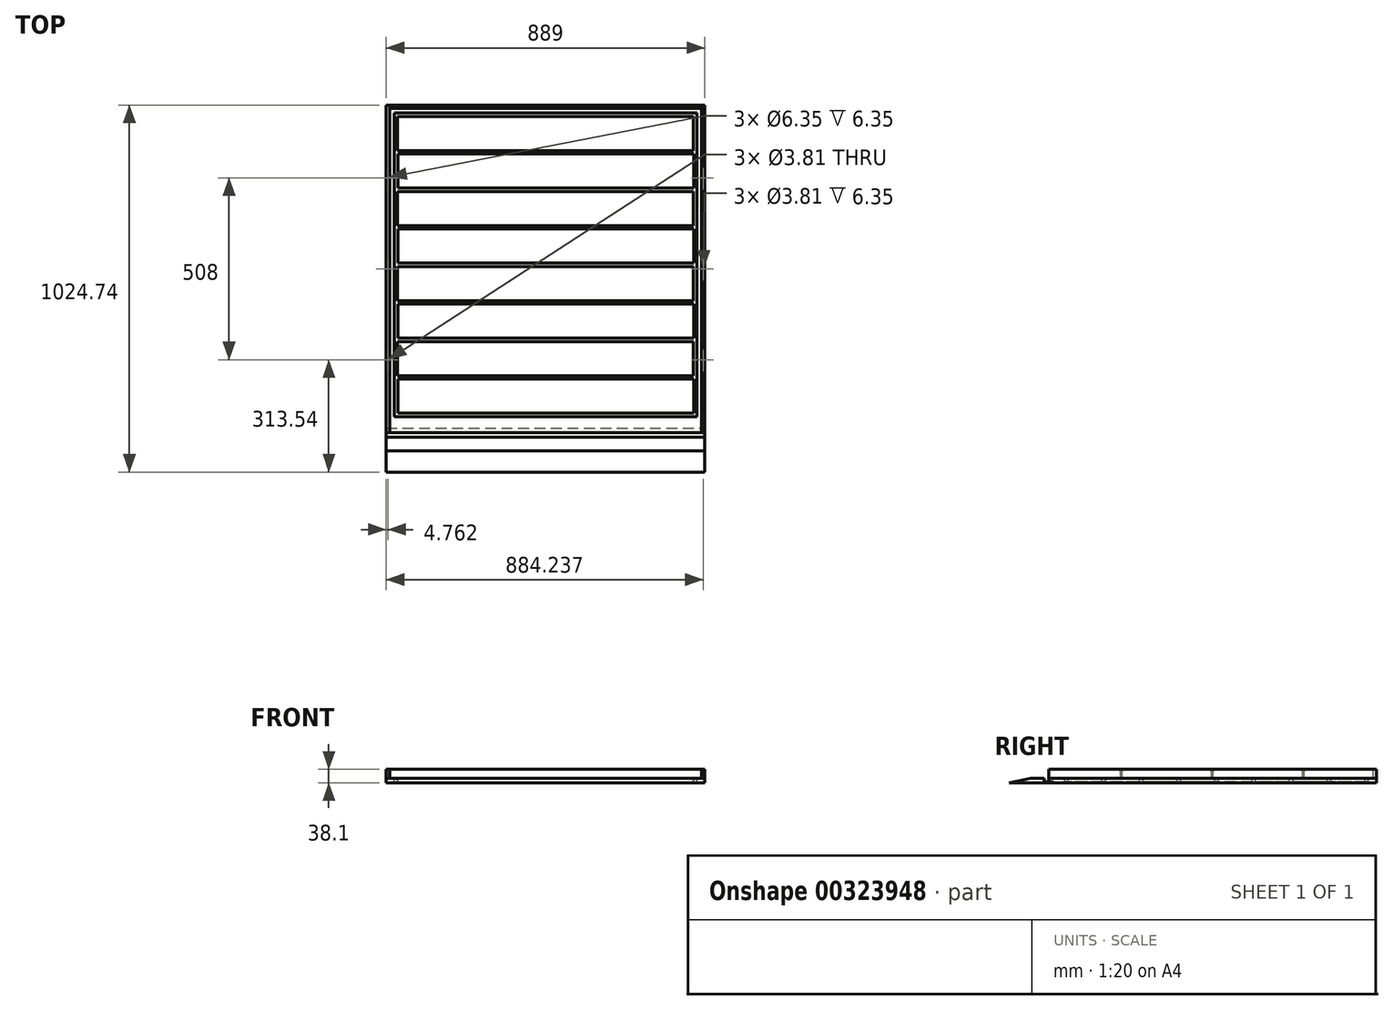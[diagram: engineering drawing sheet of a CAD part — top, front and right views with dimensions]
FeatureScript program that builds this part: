
annotation { "Feature Type Name" : "Feature", "Feature Type Description" : "" }
export const myFeature = defineFeature(function(context is Context, id is Id, definition is map)
    precondition{}
    {
        {
            var Q0;
            Q0=qCreatedBy(makeId("Top.planeOp"),FACE);
            var sketch = newSketch(context, id + "F0", { "sketchPlane" : qUnion([Q0])});
            skLineSegment(sketch, "E0.bottom", {"start": v(-444.5, 457.2) * mm, "end": v(444.5, 457.2) * mm});
            skLineSegment(sketch, "E0.top", {"start": v(-444.5, -457.2) * mm, "end": v(444.5, -457.2) * mm});
            skLineSegment(sketch, "E0.left", {"start": v(-444.5, 457.2) * mm, "end": v(-444.5, -457.2) * mm});
            skLineSegment(sketch, "E0.right", {"start": v(444.5, 457.2) * mm, "end": v(444.5, -457.2) * mm});
            skSolve(sketch);
        }
        {
            var Q0;
            Q0=makeQuery(id+"F0.imprint","IMPRINT",FACE,{"disambiguationData":[TD([[makeQuery(id+"F0.imprint","IMPRINT",EDGE,{"derivedFrom":sQuery(id+"F0.wireOp",EDGE,"E0.bottom")}),-1.0]])]});
            extrude(context, id + "F1", {"entities" : qUnion([Q0]), "depth" : 12.7 * mm});
        }
        {
            var Q0;
            Q0=makeQuery(id+"F1.opExtrude","SWEPT_FACE",FACE,{"disambiguationData":[OSD([sQuery(id+"F0.wireOp",EDGE,"E0.right")])]});
            var sketch = newSketch(context, id + "F2", { "sketchPlane" : qUnion([Q0])});
            skLineSegment(sketch, "E1", {"start": v(-457.2, 0) * mm, "end": v(-457.2, 3.17) * mm});
            skLineSegment(sketch, "E2", {"start": v(-457.2, 3.17) * mm, "end": v(-444.5, 3.17) * mm});
            skLineSegment(sketch, "E3", {"start": v(-444.5, 3.17) * mm, "end": v(-444.5, 0) * mm});
            skLineSegment(sketch, "E4", {"start": v(-457.2, 0) * mm, "end": v(-444.5, 0) * mm});
            skSolve(sketch);
        }
        {
            var Q0;
            Q0=makeQuery(id+"F2.imprint","IMPRINT",FACE,{"disambiguationData":[TD([[makeQuery(id+"F2.imprint","IMPRINT",EDGE,{"derivedFrom":sQuery(id+"F2.wireOp",EDGE,"E1")}),1.0]])]});
            extrude(context, id + "F3", {"entities" : qUnion([Q0]), "operationType" : NewBodyOperationType.REMOVE, "endBound" : BoundingType.THROUGH_ALL, "oppositeDirection" : true, "depth" : 25.4 * mm});
        }
        {
            var Q0;
            Q0=makeQuery(id+"F1.opExtrude","SWEPT_FACE",FACE,{"disambiguationData":[OSD([sQuery(id+"F0.wireOp",EDGE,"E0.right")])]});
            var sketch = newSketch(context, id + "F4", { "sketchPlane" : qUnion([Q0])});
            skLineSegment(sketch, "E5", {"start": v(-508, 12.7) * mm, "end": v(-567.54, 0) * mm});
            skLineSegment(sketch, "E6", {"start": v(-469.9, 12.7) * mm, "end": v(-469.9, 3.18) * mm});
            skLineSegment(sketch, "E7", {"start": v(-508, 12.7) * mm, "end": v(-469.9, 12.7) * mm});
            skLineSegment(sketch, "E8", {"start": v(-469.9, 3.18) * mm, "end": v(-444.5, 3.18) * mm});
            skLineSegment(sketch, "E9", {"start": v(-444.5, 3.18) * mm, "end": v(-444.5, 0) * mm});
            skLineSegment(sketch, "E10", {"start": v(-444.5, 0) * mm, "end": v(-567.54, 0) * mm});
            skSolve(sketch);
        }
        {
            var Q0;
            Q0=makeQuery(id+"F4.imprint","IMPRINT",FACE,{"disambiguationData":[TD([[makeQuery(id+"F4.imprint","IMPRINT",EDGE,{"derivedFrom":sQuery(id+"F4.wireOp",EDGE,"E5")}),1.0]])]});
            var Q1;
            Q1=makeQuery(id+"F1.opExtrude","SWEPT_FACE",FACE,{"disambiguationData":[OSD([sQuery(id+"F0.wireOp",EDGE,"E0.left")])]});
            extrude(context, id + "F5", {"entities" : qUnion([Q0]), "endBound" : BoundingType.UP_TO_SURFACE, "oppositeDirection" : true, "endBoundEntityFace" : qUnion([Q1]), "depth" : 25.4 * mm});
        }
        {
            var Q0;
            Q0=makeQuery(id+"F1.opExtrude","CAP_FACE",FACE,{"disambiguationData":[OSD([sQuery(id+"F0.wireOp",EDGE,"E0.bottom"),sQuery(id+"F0.wireOp",EDGE,"E0.top"),sQuery(id+"F0.wireOp",EDGE,"E0.left"),sQuery(id+"F0.wireOp",EDGE,"E0.right")])],"isStart":false});
            var sketch = newSketch(context, id + "F6", { "sketchPlane" : qUnion([Q0])});
            skLineSegment(sketch, "E11.bottom", {"start": v(444.5, -457.2) * mm, "end": v(434.98, -457.2) * mm});
            skLineSegment(sketch, "E11.top", {"start": v(444.5, 457.2) * mm, "end": v(434.98, 457.2) * mm});
            skLineSegment(sketch, "E11.left", {"start": v(444.5, -457.2) * mm, "end": v(444.5, 457.2) * mm});
            skLineSegment(sketch, "E11.right", {"start": v(434.98, -457.2) * mm, "end": v(434.98, 457.2) * mm});
            skLineSegment(sketch, "E12.bottom", {"start": v(-444.5, -457.2) * mm, "end": v(-434.98, -457.2) * mm});
            skLineSegment(sketch, "E12.top", {"start": v(-444.5, 457.2) * mm, "end": v(-434.98, 457.2) * mm});
            skLineSegment(sketch, "E12.left", {"start": v(-444.5, -457.2) * mm, "end": v(-444.5, 457.2) * mm});
            skLineSegment(sketch, "E12.right", {"start": v(-434.98, -457.2) * mm, "end": v(-434.98, 457.2) * mm});
            skLineSegment(sketch, "E13.bottom", {"start": v(-434.98, 457.2) * mm, "end": v(434.98, 457.2) * mm});
            skLineSegment(sketch, "E13.top", {"start": v(-434.98, 447.68) * mm, "end": v(434.98, 447.68) * mm});
            skLineSegment(sketch, "E13.left", {"start": v(-434.98, 457.2) * mm, "end": v(-434.98, 447.68) * mm});
            skLineSegment(sketch, "E13.right", {"start": v(434.98, 457.2) * mm, "end": v(434.98, 447.68) * mm});
            skSolve(sketch);
        }
        {
            var Q0;
            Q0=makeQuery(id+"F6.imprint","IMPRINT",FACE,{"disambiguationData":[TD([[makeQuery(id+"F6.imprint","IMPRINT",EDGE,{"derivedFrom":sQuery(id+"F6.wireOp",EDGE,"E11.bottom")}),1.0]])]});
            extrude(context, id + "F7", {"entities" : qUnion([Q0]), "depth" : 25.4 * mm});
        }
        {
            var Q0;
            Q0=makeQuery(id+"F6.imprint","IMPRINT",FACE,{"disambiguationData":[TD([[makeQuery(id+"F6.imprint","IMPRINT",EDGE,{"derivedFrom":sQuery(id+"F6.wireOp",EDGE,"E12.bottom")}),1.0]])]});
            extrude(context, id + "F8", {"entities" : qUnion([Q0]), "depth" : 25.4 * mm});
        }
        {
            var Q0;
            Q0=makeQuery(id+"F6.imprint","IMPRINT",FACE,{"disambiguationData":[TD([[makeQuery(id+"F6.imprint","IMPRINT",EDGE,{"derivedFrom":sQuery(id+"F6.wireOp",EDGE,"E13.bottom")}),-1.0]])]});
            extrude(context, id + "F9", {"entities" : qUnion([Q0]), "depth" : 25.4 * mm});
        }
        {
            var Q0;
            {var subQ0=sQuery(id+"F6.wireOp",EDGE,"E11.right");Q0=makeQuery(id+"F6.imprint","IMPRINT",FACE,{"disambiguationData":[TD([[makeQuery(id+"F6.imprint","IMPRINT",EDGE,{"derivedFrom":subQ0}),1.0]])]});}
            var sketch = newSketch(context, id + "F10", { "sketchPlane" : qUnion([Q0])});
            skLineSegment(sketch, "E14.bottom", {"start": v(-422.28, 434.98) * mm, "end": v(422.28, 434.98) * mm});
            skLineSegment(sketch, "E14.top", {"start": v(-422.28, -412.75) * mm, "end": v(422.28, -412.75) * mm});
            skLineSegment(sketch, "E14.left", {"start": v(-422.28, 434.98) * mm, "end": v(-422.28, -412.75) * mm});
            skLineSegment(sketch, "E14.right", {"start": v(422.28, 434.98) * mm, "end": v(422.28, -412.75) * mm});
            skLineSegment(sketch, "E15.0", {"start": v(-412.75, 425.45) * mm, "end": v(-412.75, 330.2) * mm});
            skLineSegment(sketch, "E15.1", {"start": v(-412.75, 425.45) * mm, "end": v(412.75, 425.45) * mm});
            skLineSegment(sketch, "E15.2", {"start": v(412.75, 425.45) * mm, "end": v(412.75, 330.2) * mm});
            skLineSegment(sketch, "E16.bottom", {"start": v(-412.75, 330.2) * mm, "end": v(412.75, 330.2) * mm});
            skLineSegment(sketch, "E17.0", {"start": v(-411.54, 320.68) * mm, "end": v(-411.54, 225.43) * mm});
            skLineSegment(sketch, "E17.1", {"start": v(-411.54, 320.68) * mm, "end": v(413.9, 320.68) * mm});
            skLineSegment(sketch, "E17.2", {"start": v(413.9, 320.68) * mm, "end": v(413.9, 225.43) * mm});
            skLineSegment(sketch, "E18.bottom", {"start": v(-411.54, 225.43) * mm, "end": v(413.9, 225.43) * mm});
            skLineSegment(sketch, "E19.0.1.0", {"start": v(-412.75, 215.9) * mm, "end": v(-412.75, 120.65) * mm});
            skLineSegment(sketch, "E19.0.1.1", {"start": v(-412.75, 215.9) * mm, "end": v(412.75, 215.9) * mm});
            skLineSegment(sketch, "E19.0.1.2", {"start": v(412.75, 215.9) * mm, "end": v(412.75, 120.65) * mm});
            skLineSegment(sketch, "E19.0.1.3", {"start": v(-412.75, 120.65) * mm, "end": v(412.75, 120.65) * mm});
            skLineSegment(sketch, "E19.0.1.4", {"start": v(-411.54, 111.13) * mm, "end": v(-411.54, 15.88) * mm});
            skLineSegment(sketch, "E19.0.1.5", {"start": v(-411.54, 111.13) * mm, "end": v(413.9, 111.13) * mm});
            skLineSegment(sketch, "E19.0.1.6", {"start": v(413.9, 111.13) * mm, "end": v(413.9, 15.88) * mm});
            skLineSegment(sketch, "E19.0.1.7", {"start": v(-411.54, 15.88) * mm, "end": v(413.9, 15.88) * mm});
            skLineSegment(sketch, "E19.0.2.0", {"start": v(-412.75, 6.35) * mm, "end": v(-412.75, -88.9) * mm});
            skLineSegment(sketch, "E19.0.2.1", {"start": v(-412.75, 6.35) * mm, "end": v(412.75, 6.35) * mm});
            skLineSegment(sketch, "E19.0.2.2", {"start": v(412.75, 6.35) * mm, "end": v(412.75, -88.9) * mm});
            skLineSegment(sketch, "E19.0.2.3", {"start": v(-412.75, -88.9) * mm, "end": v(412.75, -88.9) * mm});
            skLineSegment(sketch, "E19.0.2.4", {"start": v(-411.54, -98.42) * mm, "end": v(-411.54, -193.67) * mm});
            skLineSegment(sketch, "E19.0.2.5", {"start": v(-411.54, -98.42) * mm, "end": v(413.9, -98.42) * mm});
            skLineSegment(sketch, "E19.0.2.6", {"start": v(413.9, -98.42) * mm, "end": v(413.9, -193.67) * mm});
            skLineSegment(sketch, "E19.0.2.7", {"start": v(-411.54, -193.67) * mm, "end": v(413.9, -193.67) * mm});
            skLineSegment(sketch, "E19.0.3.0", {"start": v(-412.75, -203.2) * mm, "end": v(-412.75, -298.45) * mm});
            skLineSegment(sketch, "E19.0.3.1", {"start": v(-412.75, -203.2) * mm, "end": v(412.75, -203.2) * mm});
            skLineSegment(sketch, "E19.0.3.2", {"start": v(412.75, -203.2) * mm, "end": v(412.75, -298.45) * mm});
            skLineSegment(sketch, "E19.0.3.3", {"start": v(-412.75, -298.45) * mm, "end": v(412.75, -298.45) * mm});
            skLineSegment(sketch, "E19.0.3.4", {"start": v(-411.54, -307.97) * mm, "end": v(-411.54, -403.22) * mm});
            skLineSegment(sketch, "E19.0.3.5", {"start": v(-411.54, -307.97) * mm, "end": v(413.9, -307.97) * mm});
            skLineSegment(sketch, "E19.0.3.6", {"start": v(413.9, -307.97) * mm, "end": v(413.9, -403.22) * mm});
            skLineSegment(sketch, "E19.0.3.7", {"start": v(-411.54, -403.22) * mm, "end": v(413.9, -403.22) * mm});
            skLineSegment(sketch, "E19.direction1", {"start": v(-411.54, 225.43) * mm, "end": v(-386.2, 225.43) * mm, "construction": true});
            skSolve(sketch);
        }
        {
            var Q0;
            Q0=makeQuery(id+"F10.imprint","IMPRINT",FACE,{"disambiguationData":[TD([[makeQuery(id+"F10.imprint","IMPRINT",EDGE,{"derivedFrom":sQuery(id+"F10.wireOp",EDGE,"E14.bottom")}),-1.0]])]});
            extrude(context, id + "F11", {"entities" : qUnion([Q0]), "operationType" : NewBodyOperationType.REMOVE, "oppositeDirection" : true, "depth" : 9.52 * mm});
        }
        {
            var Q0;
            Q0=makeQuery(id+"F8.opExtrude","CAP_FACE",FACE,{"disambiguationData":[OSD([sQuery(id+"F6.wireOp",EDGE,"E12.bottom"),sQuery(id+"F6.wireOp",EDGE,"E12.top"),sQuery(id+"F6.wireOp",EDGE,"E12.left"),sQuery(id+"F6.wireOp",EDGE,"E12.right"),sQuery(id+"F6.wireOp",EDGE,"E13.left")])],"isStart":false});
            var sketch = newSketch(context, id + "F12", { "sketchPlane" : qUnion([Q0])});
            skSolve(sketch);
        }
        {
            var Q0;
            Q0=makeQuery(id+"F12.imprint","IMPRINT",FACE,{"disambiguationData":[TD([[makeQuery(id+"F12.imprint","IMPRINT",EDGE,{"derivedFrom":makeQuery(id+"F8.opExtrude","CAP_EDGE",EDGE,{"disambiguationData":[OSD([sQuery(id+"F6.wireOp",EDGE,"E12.bottom")])],"isStart":false})}),1.0]])]});
            var sketch = newSketch(context, id + "F13", { "sketchPlane" : qUnion([Q0])});
            skCircle(sketch, "E20", {"center": v(-439.74, 254) * mm, "radius": 3.18 * mm});
            skCircle(sketch, "E21", {"center": v(-439.74, 254) * mm, "radius": 1.9 * mm});
            skCircle(sketch, "E22", {"center": v(-439.74, 0) * mm, "radius": 3.18 * mm});
            skCircle(sketch, "E23", {"center": v(-439.74, 0) * mm, "radius": 1.9 * mm});
            skCircle(sketch, "E24", {"center": v(-439.74, -254) * mm, "radius": 3.18 * mm});
            skCircle(sketch, "E25", {"center": v(-439.74, -254) * mm, "radius": 1.9 * mm});
            skCircle(sketch, "E26.MirrorC", {"center": v(439.74, -254) * mm, "radius": 1.9 * mm});
            skCircle(sketch, "E27.MirrorC", {"center": v(439.74, -254) * mm, "radius": 3.18 * mm});
            skCircle(sketch, "E28.MirrorC", {"center": v(439.74, 0) * mm, "radius": 1.9 * mm});
            skCircle(sketch, "E29.MirrorC", {"center": v(439.74, 0) * mm, "radius": 3.18 * mm});
            skCircle(sketch, "E30.MirrorC", {"center": v(439.74, 254) * mm, "radius": 1.9 * mm});
            skCircle(sketch, "E31.MirrorC", {"center": v(439.74, 254) * mm, "radius": 3.18 * mm});
            skSolve(sketch);
        }
        {
            var Q0;
            Q0=makeQuery(id+"F13.imprint","IMPRINT",FACE,{"disambiguationData":[TD([[makeQuery(id+"F13.imprint","IMPRINT",EDGE,{"derivedFrom":sQuery(id+"F13.wireOp",EDGE,"E24")}),1.0]])]});
            var Q1;
            Q1=makeQuery(id+"F13.imprint","IMPRINT",FACE,{"disambiguationData":[TD([[makeQuery(id+"F13.imprint","IMPRINT",EDGE,{"derivedFrom":sQuery(id+"F13.wireOp",EDGE,"E22")}),1.0]])]});
            var Q2;
            Q2=makeQuery(id+"F13.imprint","IMPRINT",FACE,{"disambiguationData":[TD([[makeQuery(id+"F13.imprint","IMPRINT",EDGE,{"derivedFrom":sQuery(id+"F13.wireOp",EDGE,"E20")}),1.0]])]});
            var Q3;
            Q3=makeQuery(id+"F13.imprint","IMPRINT",FACE,{"disambiguationData":[TD([[makeQuery(id+"F13.imprint","IMPRINT",EDGE,{"derivedFrom":sQuery(id+"F13.wireOp",EDGE,"E30.MirrorC")}),1.0]])]});
            var Q4;
            Q4=makeQuery(id+"F13.imprint","IMPRINT",FACE,{"disambiguationData":[TD([[makeQuery(id+"F13.imprint","IMPRINT",EDGE,{"derivedFrom":sQuery(id+"F13.wireOp",EDGE,"E28.MirrorC")}),1.0]])]});
            var Q5;
            Q5=makeQuery(id+"F13.imprint","IMPRINT",FACE,{"disambiguationData":[TD([[makeQuery(id+"F13.imprint","IMPRINT",EDGE,{"derivedFrom":sQuery(id+"F13.wireOp",EDGE,"E26.MirrorC")}),1.0]])]});
            extrude(context, id + "F14", {"entities" : qUnion([Q0, Q1, Q2, Q3, Q4, Q5]), "operationType" : NewBodyOperationType.REMOVE, "oppositeDirection" : true, "depth" : 6.35 * mm});
        }
        {
            var Q0;
            Q0=makeQuery(id+"F14.boolean.opBoolean","SPLIT",FACE,{"disambiguationData":[TD([makeQuery(id+"F14.opExtrude","SWEPT_FACE",FACE,{"disambiguationData":[OSD([sQuery(id+"F13.wireOp",EDGE,"E25")])]})])],"derivedFrom":makeQuery(id+"F8.opExtrude","CAP_FACE",FACE,{"disambiguationData":[OSD([sQuery(id+"F6.wireOp",EDGE,"E12.bottom"),sQuery(id+"F6.wireOp",EDGE,"E12.top"),sQuery(id+"F6.wireOp",EDGE,"E12.left"),sQuery(id+"F6.wireOp",EDGE,"E12.right"),sQuery(id+"F6.wireOp",EDGE,"E13.left")])],"isStart":false})});
            var Q1;
            Q1=makeQuery(id+"F14.boolean.opBoolean","SPLIT",FACE,{"disambiguationData":[TD([makeQuery(id+"F14.opExtrude","SWEPT_FACE",FACE,{"disambiguationData":[OSD([sQuery(id+"F13.wireOp",EDGE,"E23")])]})])],"derivedFrom":makeQuery(id+"F8.opExtrude","CAP_FACE",FACE,{"disambiguationData":[OSD([sQuery(id+"F6.wireOp",EDGE,"E12.bottom"),sQuery(id+"F6.wireOp",EDGE,"E12.top"),sQuery(id+"F6.wireOp",EDGE,"E12.left"),sQuery(id+"F6.wireOp",EDGE,"E12.right"),sQuery(id+"F6.wireOp",EDGE,"E13.left")])],"isStart":false})});
            var Q2;
            Q2=makeQuery(id+"F14.boolean.opBoolean","SPLIT",FACE,{"disambiguationData":[TD([makeQuery(id+"F14.opExtrude","SWEPT_FACE",FACE,{"disambiguationData":[OSD([sQuery(id+"F13.wireOp",EDGE,"E21")])]})])],"derivedFrom":makeQuery(id+"F8.opExtrude","CAP_FACE",FACE,{"disambiguationData":[OSD([sQuery(id+"F6.wireOp",EDGE,"E12.bottom"),sQuery(id+"F6.wireOp",EDGE,"E12.top"),sQuery(id+"F6.wireOp",EDGE,"E12.left"),sQuery(id+"F6.wireOp",EDGE,"E12.right"),sQuery(id+"F6.wireOp",EDGE,"E13.left")])],"isStart":false})});
            var Q3;
            Q3=makeQuery(id+"F8.opExtrude","CAP_FACE",FACE,{"disambiguationData":[OSD([sQuery(id+"F6.wireOp",EDGE,"E12.bottom"),sQuery(id+"F6.wireOp",EDGE,"E12.top"),sQuery(id+"F6.wireOp",EDGE,"E12.left"),sQuery(id+"F6.wireOp",EDGE,"E12.right"),sQuery(id+"F6.wireOp",EDGE,"E13.left")])],"isStart":true});
            extrude(context, id + "F15", {"entities" : qUnion([Q0, Q1, Q2]), "operationType" : NewBodyOperationType.REMOVE, "endBound" : BoundingType.UP_TO_SURFACE, "oppositeDirection" : true, "endBoundEntityFace" : qUnion([Q3]), "depth" : 25.4 * mm});
        }
    });
